# Revit family: Storage-Teknion-LWBRS_Byward_Return_with_Storage-R2019
name_source: partatom
category: Furniture
units: mm (PartAtom-declared; Revit-internal decimal feet)

## family parameters
Always vertical = Yes
Cut with Voids When Loaded = No
OmniClass Number = 23.40.20.00
OmniClass Title = General Furniture and Specialties
Room Calculation Point = No
Shared = Yes
Work Plane-Based = No

## types (4) — shared parameters
Assembly Code = E2020200
Manufacturer = Teknion
Manufacturer Fax = 416.661.4586
Part Number = LWBRS
Product Documentation Link = https://assets.teknion.com
Product Line = Byward
Product Page URL = https://www.teknion.com
Series = Byward
Sustainability Data = https://www.teknion.com
URL = www.teknion.com
Unit Weight URL = http://www.teknion.com
Warranty = http://www.teknion.com

## per-type parameters (varying)
| type | Description | Model | Width |
| 14" Depth, 36" Width | Byward Return with Storage, 14" Depth, 36" Width | LWBRS1436_ | 36 " |
| 14" Depth, 48" Width | Byward Return with Storage, 14" Depth, 48" Width | LWBRS1448_ | 48 " |
| 14" Depth, 54" Width | Byward Return with Storage, 14" Depth, 54" Width | LWBRS1454_ | 54 " |
| 14" Depth, 60" Width | Byward Return with Storage, 14" Depth, 60" Width | LWBRS1460_ | 60 " |

## geometry (parser evidence)
native form markers: Sweep x3
no freeform markers — native parametric forms only
